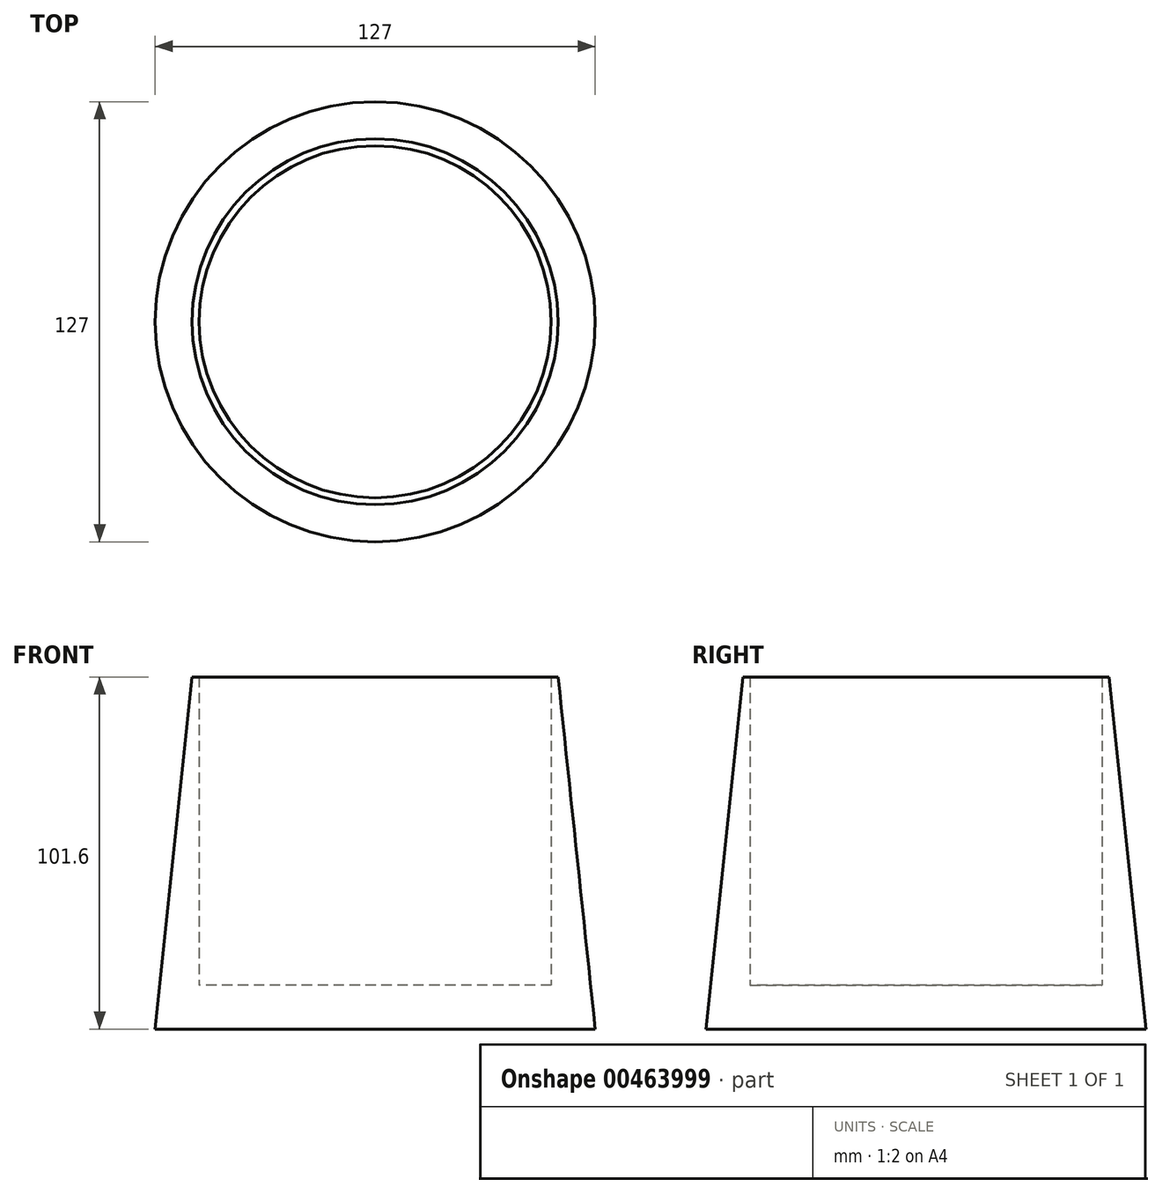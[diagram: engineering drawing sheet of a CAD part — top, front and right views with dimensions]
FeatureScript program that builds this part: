
annotation { "Feature Type Name" : "Feature", "Feature Type Description" : "" }
export const myFeature = defineFeature(function(context is Context, id is Id, definition is map)
    precondition{}
    {
        {
            var Q0;
            Q0=qCreatedBy(makeId("Top.planeOp"),FACE);
            var sketch = newSketch(context, id + "F0", { "sketchPlane" : qUnion([Q0])});
            skCircle(sketch, "E0", {"center": v(0, 0) * mm, "radius": 63.5 * mm});
            skCircle(sketch, "E1.0", {"center": v(0, 0) * mm, "radius": 50.8 * mm});
            skSolve(sketch);
        }
        {
            var Q0;
            Q0=makeQuery(id+"F0.imprint","IMPRINT",FACE,{"disambiguationData":[TD([[makeQuery(id+"F0.imprint","IMPRINT",EDGE,{"derivedFrom":sQuery(id+"F0.wireOp",EDGE,"E0")}),1.0]])]});
            extrude(context, id + "F1", {"entities" : qUnion([Q0]), "depth" : 101.6 * mm, "offsetDistance" : 25.4 * mm});
        }
        {
            var Q0;
            Q0=makeQuery(id+"F0.imprint","IMPRINT",FACE,{"disambiguationData":[TD([[makeQuery(id+"F0.imprint","IMPRINT",EDGE,{"derivedFrom":sQuery(id+"F0.wireOp",EDGE,"E1.0")}),1.0]])]});
            extrude(context, id + "F2", {"entities" : qUnion([Q0]), "operationType" : NewBodyOperationType.ADD, "depth" : 12.7 * mm});
        }
        {
            var Q0;
            Q0=makeQuery(id+"F1.opExtrude","CAP_EDGE",EDGE,{"disambiguationData":[OSD([sQuery(id+"F0.wireOp",EDGE,"E0")])],"isStart":false});
            chamfer(context, id + "F3", {"entities" : qUnion([Q0]), "chamferType" : ChamferType.OFFSET_ANGLE, "width" : 101.6 * mm, "oppositeDirection" : true, "angle" : 6 * degree, "tangentPropagation" : true});
        }
    });
